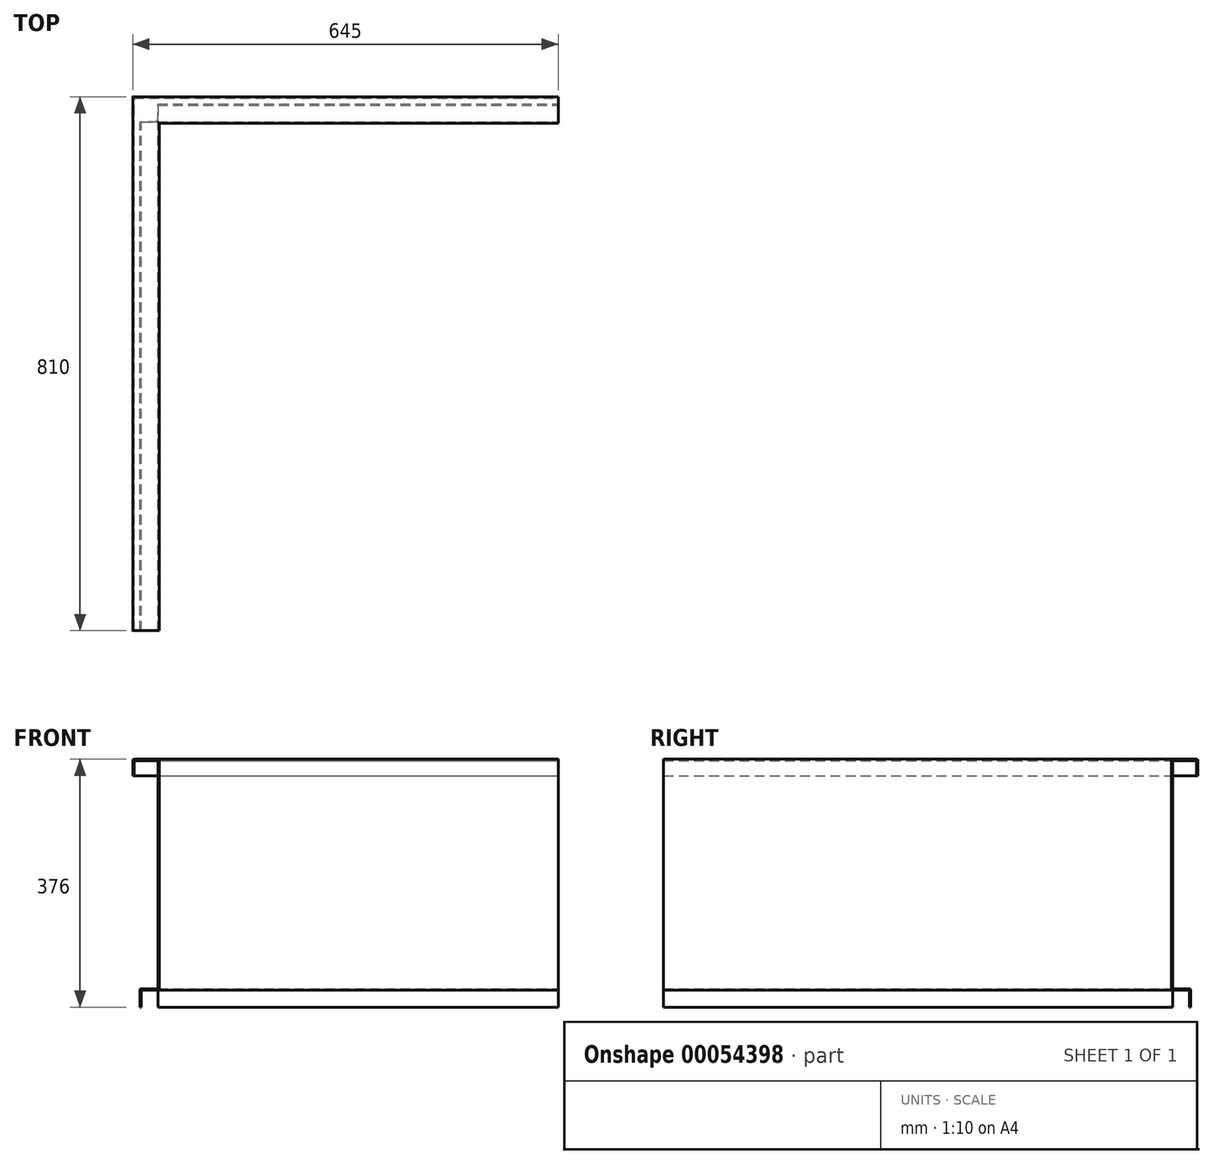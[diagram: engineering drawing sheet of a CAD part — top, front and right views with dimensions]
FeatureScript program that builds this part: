
annotation { "Feature Type Name" : "Feature", "Feature Type Description" : "" }
export const myFeature = defineFeature(function(context is Context, id is Id, definition is map)
    precondition{}
    {
        {
            var Q0;
            Q0=qCreatedBy(makeId("Front.planeOp"),FACE);
            var sketch = newSketch(context, id + "F0", { "sketchPlane" : qUnion([Q0])});
            skLineSegment(sketch, "E0", {"start": v(0, 0) * mm, "end": v(0, -350) * mm});
            skLineSegment(sketch, "E1", {"start": v(0, -350) * mm, "end": v(-27, -350) * mm});
            skLineSegment(sketch, "E2", {"start": v(-27, -350) * mm, "end": v(-27, -376) * mm});
            skLineSegment(sketch, "E3", {"start": v(0, 0) * mm, "end": v(-40, 0) * mm});
            skLineSegment(sketch, "E4", {"start": v(-40, 0) * mm, "end": v(-40, -25) * mm});
            skLineSegment(sketch, "E5.0", {"start": v(-38, -2) * mm, "end": v(-38, -25) * mm});
            skLineSegment(sketch, "E5.1", {"start": v(-29, -348) * mm, "end": v(-29, -376) * mm});
            skLineSegment(sketch, "E5.2", {"start": v(-2, -348) * mm, "end": v(-29, -348) * mm});
            skLineSegment(sketch, "E5.3", {"start": v(-2, -2) * mm, "end": v(-2, -348) * mm});
            skLineSegment(sketch, "E5.4", {"start": v(-2, -2) * mm, "end": v(-38, -2) * mm});
            skLineSegment(sketch, "E6", {"start": v(-40, -25) * mm, "end": v(-38, -25) * mm});
            skLineSegment(sketch, "E7", {"start": v(-29, -376) * mm, "end": v(-27, -376) * mm});
            skSolve(sketch);
        }
        {
            var Q0;
            Q0=qCreatedBy(makeId("Top.planeOp"),FACE);
            var sketch = newSketch(context, id + "F1", { "sketchPlane" : qUnion([Q0])});
            skLineSegment(sketch, "E8", {"start": v(0, 0) * mm, "end": v(0, 770) * mm});
            skLineSegment(sketch, "E9", {"start": v(0, 770) * mm, "end": v(605, 770) * mm});
            skSolve(sketch);
        }
        {
            var Q0;
            Q0=qSketchRegion(id+"F0",true);
            var Q1;
            Q1=qConstructionFilter(qBodyType(qCreatedBy(id+"F1",EDGE),BodyType.WIRE),ConstructionObject.NO);
            sweep(context, id + "F2", {"profiles" : qUnion([Q0]), "path" : qUnion([Q1])});
        }
        {
            var Q0;
            Q0=makeQuery(id+"F2.opSweep","SWEPT_FACE",FACE,{"disambiguationData":[OSD([sQuery(id+"F0.wireOp",EDGE,"E5.2"),sQuery(id+"F1.wireOp",EDGE,"E8")])]});
            var sketch = newSketch(context, id + "F3", { "sketchPlane" : qUnion([Q0])});
            skLineSegment(sketch, "E10", {"start": v(-2, 772) * mm, "end": v(-29, 772) * mm});
            skLineSegment(sketch, "E11", {"start": v(-29, 772) * mm, "end": v(-29, 799) * mm});
            skLineSegment(sketch, "E12", {"start": v(-29, 799) * mm, "end": v(-2, 799) * mm});
            skLineSegment(sketch, "E13", {"start": v(-2, 799) * mm, "end": v(-2, 772) * mm});
            skSolve(sketch);
        }
        {
            var Q0;
            Q0 = qSketchRegion(id + "F3", true);
            extrude(context, id + "F4", {"entities" : qUnion([Q0]), "operationType" : NewBodyOperationType.REMOVE, "oppositeDirection" : true, "depth" : 30 * mm});
        }
        {
            var Q0;
            Q0=makeQuery(id+"F2.opSweep","SWEPT_EDGE",EDGE,{"disambiguationData":[OSD([sQuery(id+"F0.wireOp",EDGE,"E5.1"),sQuery(id+"F0.wireOp",EDGE,"E5.2"),sQuery(id+"F1.wireOp",EDGE,"E9")])]});
            var Q1;
            Q1=makeQuery(id+"F2.opSweep","SWEPT_EDGE",EDGE,{"disambiguationData":[OSD([sQuery(id+"F0.wireOp",EDGE,"E5.2"),sQuery(id+"F0.wireOp",EDGE,"E5.3"),sQuery(id+"F1.wireOp",EDGE,"E9")])]});
            var Q2;
            Q2=makeQuery(id+"F2.opSweep","SWEPT_EDGE",EDGE,{"disambiguationData":[OSD([sQuery(id+"F0.wireOp",EDGE,"E5.1"),sQuery(id+"F0.wireOp",EDGE,"E5.2"),sQuery(id+"F1.wireOp",EDGE,"E8")])]});
            var Q3;
            Q3=makeQuery(id+"F2.opSweep","SWEPT_EDGE",EDGE,{"disambiguationData":[OSD([sQuery(id+"F0.wireOp",EDGE,"E3"),sQuery(id+"F0.wireOp",EDGE,"E4"),sQuery(id+"F1.wireOp",EDGE,"E8")])]});
            var Q4;
            Q4=makeQuery(id+"F2.opSweep","SWEPT_EDGE",EDGE,{"disambiguationData":[OSD([sQuery(id+"F0.wireOp",EDGE,"E0"),sQuery(id+"F0.wireOp",EDGE,"E3"),sQuery(id+"F1.wireOp",EDGE,"E8")])]});
            var Q5;
            Q5=makeQuery(id+"F2.opSweep","SWEPT_EDGE",EDGE,{"disambiguationData":[OSD([sQuery(id+"F0.wireOp",EDGE,"E0"),sQuery(id+"F0.wireOp",EDGE,"E3"),sQuery(id+"F1.wireOp",EDGE,"E9")])]});
            var Q6;
            Q6=makeQuery(id+"F2.opSweep","SWEPT_EDGE",EDGE,{"disambiguationData":[OSD([sQuery(id+"F0.wireOp",EDGE,"E3"),sQuery(id+"F0.wireOp",EDGE,"E4"),sQuery(id+"F1.wireOp",EDGE,"E9")])]});
            var Q7;
            Q7=makeQuery(id+"F2.opSweep","SWEPT_EDGE",EDGE,{"disambiguationData":[OSD([sQuery(id+"F0.wireOp",EDGE,"E5.3"),sQuery(id+"F0.wireOp",EDGE,"E5.4"),sQuery(id+"F1.wireOp",EDGE,"E8")])]});
            var Q8;
            Q8=makeQuery(id+"F2.opSweep","SWEPT_EDGE",EDGE,{"disambiguationData":[OSD([sQuery(id+"F0.wireOp",EDGE,"E5.3"),sQuery(id+"F0.wireOp",EDGE,"E5.4"),sQuery(id+"F1.wireOp",EDGE,"E9")])]});
            var Q9;
            Q9=makeQuery(id+"F2.opSweep","SWEPT_EDGE",EDGE,{"disambiguationData":[OSD([sQuery(id+"F0.wireOp",EDGE,"E5.0"),sQuery(id+"F0.wireOp",EDGE,"E5.4"),sQuery(id+"F1.wireOp",EDGE,"E8")])]});
            var Q10;
            Q10=makeQuery(id+"F2.opSweep","SWEPT_EDGE",EDGE,{"disambiguationData":[OSD([sQuery(id+"F0.wireOp",EDGE,"E5.0"),sQuery(id+"F0.wireOp",EDGE,"E5.4"),sQuery(id+"F1.wireOp",EDGE,"E9")])]});
            var Q11;
            Q11=makeQuery(id+"F2.opSweep","SWEPT_EDGE",EDGE,{"disambiguationData":[OSD([sQuery(id+"F0.wireOp",EDGE,"E1"),sQuery(id+"F0.wireOp",EDGE,"E2"),sQuery(id+"F1.wireOp",EDGE,"E9")])]});
            var Q12;
            Q12=makeQuery(id+"F2.opSweep","SWEPT_EDGE",EDGE,{"disambiguationData":[OSD([sQuery(id+"F0.wireOp",EDGE,"E0"),sQuery(id+"F0.wireOp",EDGE,"E1"),sQuery(id+"F1.wireOp",EDGE,"E9")])]});
            var Q13;
            Q13=makeQuery(id+"F2.opSweep","SWEPT_EDGE",EDGE,{"disambiguationData":[OSD([sQuery(id+"F0.wireOp",EDGE,"E0"),sQuery(id+"F0.wireOp",EDGE,"E1"),sQuery(id+"F1.wireOp",EDGE,"E8")])]});
            var Q14;
            Q14=makeQuery(id+"F2.opSweep","SWEPT_EDGE",EDGE,{"disambiguationData":[OSD([sQuery(id+"F0.wireOp",EDGE,"E1"),sQuery(id+"F0.wireOp",EDGE,"E2"),sQuery(id+"F1.wireOp",EDGE,"E8")])]});
            fillet(context, id + "F5", {"entities" : qUnion([Q0, Q1, Q2, Q3, Q4, Q5, Q6, Q7, Q8, Q9, Q10, Q11, Q12, Q13, Q14]), "radius" : 2 * mm, "tangentPropagation" : true, "allowEdgeOverflow" : false});
        }
    });
